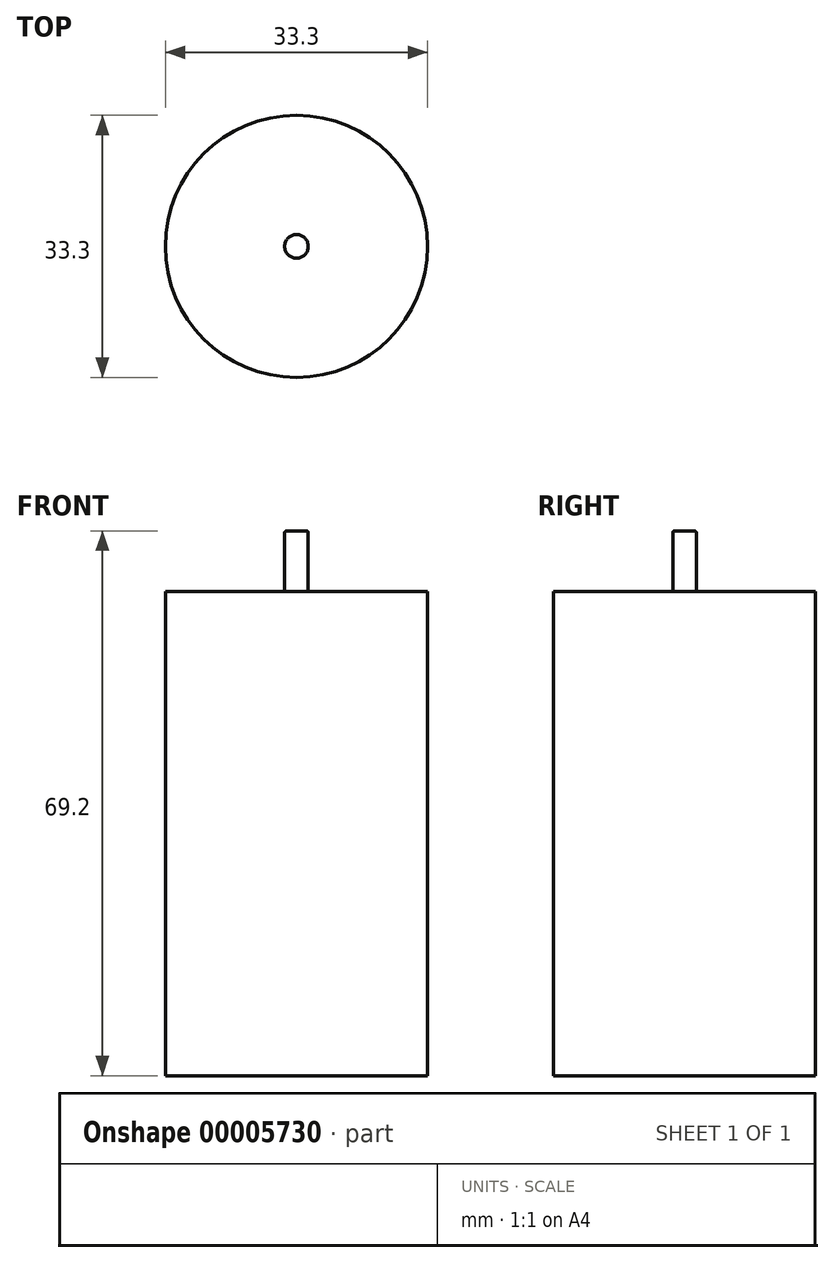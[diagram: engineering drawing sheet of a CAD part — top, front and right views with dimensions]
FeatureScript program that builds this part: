
annotation { "Feature Type Name" : "Feature", "Feature Type Description" : "" }
export const myFeature = defineFeature(function(context is Context, id is Id, definition is map)
    precondition{}
    {
        {
            var Q0;
            Q0=qCreatedBy(makeId("Top.planeOp"),FACE);
            var sketch = newSketch(context, id + "F0", { "sketchPlane" : qUnion([Q0])});
            skCircle(sketch, "E0", {"center": v(0, 0) * mm, "radius": 16.65 * mm});
            skSolve(sketch);
        }
        {
            var Q0;
            Q0=makeQuery(id+"F0.imprint","IMPRINT",FACE,{"disambiguationData":[TD([[makeQuery(id+"F0.imprint","IMPRINT",EDGE,{"derivedFrom":sQuery(id+"F0.wireOp",EDGE,"E0")}),1.0]])]});
            extrude(context, id + "F1", {"entities" : qUnion([Q0]), "depth" : 61.5 * mm});
        }
        {
            var Q0;
            Q0=makeQuery(id+"F1.opExtrude","CAP_FACE",FACE,{"disambiguationData":[OSD([sQuery(id+"F0.wireOp",EDGE,"E0")])],"isStart":false});
            var sketch = newSketch(context, id + "F2", { "sketchPlane" : qUnion([Q0])});
            skCircle(sketch, "E1", {"center": v(0, 0) * mm, "radius": 1.5 * mm});
            skSolve(sketch);
        }
        {
            var Q0;
            Q0=makeQuery(id+"F2.imprint","IMPRINT",FACE,{"disambiguationData":[TD([[makeQuery(id+"F2.imprint","IMPRINT",EDGE,{"derivedFrom":sQuery(id+"F2.wireOp",EDGE,"E1")}),1.0]])]});
            extrude(context, id + "F3", {"entities" : qUnion([Q0]), "operationType" : NewBodyOperationType.ADD, "depth" : 7.7 * mm});
        }
        {
            var Q0;
            Q0=makeQuery(id+"F3.opExtrude","CAP_EDGE",EDGE,{"disambiguationData":[OSD([sQuery(id+"F2.wireOp",EDGE,"E1")])],"isStart":false});
            fillet(context, id + "F4", {"entities" : qUnion([Q0]), "radius" : 0.25 * mm, "tangentPropagation" : true, "allowEdgeOverflow" : false});
        }
    });
